# Revit family: ADB Electric Gastronorm range cookers L1000
name_source: partatom
category: Equipement spécialisé
units: mm (PartAtom-declared; Revit-internal decimal feet)

## family parameters
Basée sur le plan de construction = Non
Conserver l'orientation des annotations = Non
Cote de connecteur circulaire = Utiliser le diamètre
Couper avec des vides une fois chargée = Non
Numéro OmniClass = 23.40.40.14.17.11
Partagée = Non
Repère de localisation dans la pièce = Non
Titre OmniClass = Cookers, Ovens, Stoves
Toujours verticalement = Oui
Type d'élément = Normal

## types (2) — shared parameters
B = 555 mm  [stored 1.82087 ft]
C = 435 mm  [stored 1.42717 ft]
Commentaires du type = Ambassade range - Electric range cookers
Fabricant = Société Industrielle de Lacanche
URL = https://www.ambassade-de-bourgogne.com
zero-valued in all types: Elévation par défaut

## per-type parameters (varying)
| type | CE 1051 E | CE 1051 VTR | Description | Modèle | Pbase | Table | Weight |
| 5 Electric hotplates , 1 gastronorm oven - CE 1051 E | Oui | Non | Electric range cooker 5 Electric hotplates , 1 gastronorm oven - CE 1051 E | CE 1051 E | 12700 W | CE1051B_CE1051E_CE1052P_5 plaques électriques | 137.00 kg |
| 5 Radiant rings, 1 gastronorm oven - CE 1051 VTR | Non | Oui | Electric range cooker 5 Radiant rings, 1 gastronorm oven - CE 1051 VTR | CE 1051 VTR | 15000 W | CE1051 VTR_CE 1052 VTR_5 foyers radiants | 110.00 kg |

note: [stored X ft] marks values corroborated as IEEE doubles in the binary element streams (Revit-internal decimal feet)
